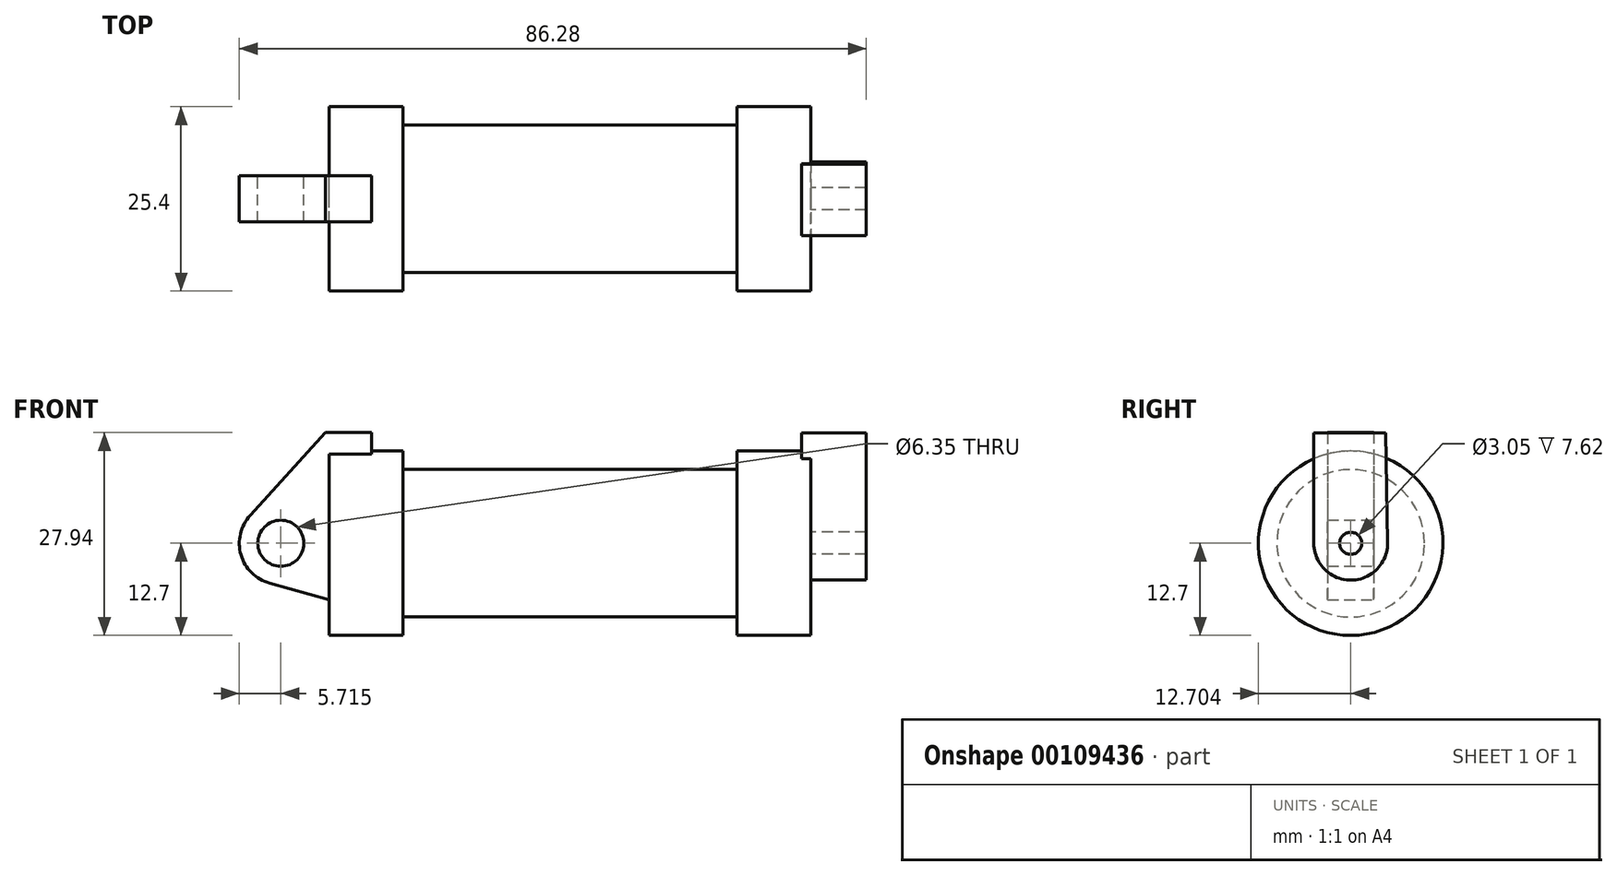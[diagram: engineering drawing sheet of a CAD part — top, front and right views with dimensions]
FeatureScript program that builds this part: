
annotation { "Feature Type Name" : "Feature", "Feature Type Description" : "" }
export const myFeature = defineFeature(function(context is Context, id is Id, definition is map)
    precondition{}
    {
        {
            var Q0;
            Q0=qCreatedBy(makeId("Front.planeOp"),FACE);
            var sketch = newSketch(context, id + "F0", { "sketchPlane" : qUnion([Q0])});
            skLineSegment(sketch, "E0", {"start": v(0, 0) * mm, "end": v(0, 12.7) * mm});
            skLineSegment(sketch, "E1", {"start": v(0, 12.7) * mm, "end": v(10.16, 12.7) * mm});
            skLineSegment(sketch, "E2", {"start": v(10.16, 12.7) * mm, "end": v(10.16, 10.16) * mm});
            skLineSegment(sketch, "E3", {"start": v(10.16, 10.16) * mm, "end": v(56.13, 10.16) * mm});
            skLineSegment(sketch, "E4", {"start": v(56.13, 10.16) * mm, "end": v(56.13, 12.7) * mm});
            skLineSegment(sketch, "E5", {"start": v(56.13, 12.7) * mm, "end": v(66.3, 12.7) * mm});
            skLineSegment(sketch, "E6", {"start": v(66.3, 12.7) * mm, "end": v(66.3, 0) * mm});
            skLineSegment(sketch, "E7", {"start": v(66.3, 0) * mm, "end": v(0, 0) * mm});
            skLineSegment(sketch, "E8", {"start": v(5.84, 15.24) * mm, "end": v(-0.5, 15.24) * mm});
            skLineSegment(sketch, "E9", {"start": v(-0.5, 15.24) * mm, "end": v(-10.88, 3.85) * mm});
            skLineSegment(sketch, "E10", {"start": v(0, 0) * mm, "end": v(-6.65, 0) * mm});
            skCircle(sketch, "E11", {"center": v(-6.65, 0) * mm, "radius": 5.72 * mm});
            skCircle(sketch, "E12", {"center": v(-6.65, 0) * mm, "radius": 3.18 * mm});
            skLineSegment(sketch, "E13", {"start": v(5.84, 15.24) * mm, "end": v(5.84, -9.4) * mm});
            skLineSegment(sketch, "E14", {"start": v(5.84, -9.4) * mm, "end": v(-8.18, -5.5) * mm});
            skSolve(sketch);
        }
        {
            var Q0;
            {var subQ0=sQuery(id+"F0.wireOp",EDGE,"E2");Q0=makeQuery(id+"F0.imprint","IMPRINT",FACE,{"disambiguationData":[TD([[makeQuery(id+"F0.imprint","IMPRINT",EDGE,{"derivedFrom":subQ0}),-1.0]])]});}
            var Q1;
            {var subQ0=sQuery(id+"F0.wireOp",EDGE,"E0");Q1=makeQuery(id+"F0.imprint","IMPRINT",FACE,{"disambiguationData":[TD([[makeQuery(id+"F0.imprint","IMPRINT",EDGE,{"derivedFrom":subQ0}),-1.0]])]});}
            var Q2;
            Q2=sQuery(id+"F0.wireOp",EDGE,"E7");
            revolve(context, id + "F1", {"entities" : qUnion([Q0, Q1]), "axis" : qUnion([Q2]), "revolveType" : RevolveType.FULL});
        }
        {
            var Q0;
            {var subQ3=sQuery(id+"F0.wireOp",EDGE,"E0");Q0=makeQuery(id+"F0.imprint","IMPRINT",FACE,{"disambiguationData":[TD([[makeQuery(id+"F0.imprint","IMPRINT",EDGE,{"derivedFrom":subQ3}),1.0]])]});}
            var Q1;
            {var subQ4=sQuery(id+"F0.wireOp",EDGE,"E12");Q1=makeQuery(id+"F0.imprint","IMPRINT",FACE,{"disambiguationData":[TD([[makeQuery(id+"F0.imprint","IMPRINT",EDGE,{"derivedFrom":subQ4}),-1.0]])]});}
            var Q2;
            {var subQ0=sQuery(id+"F0.wireOp",EDGE,"E14");Q2=makeQuery(id+"F0.imprint","IMPRINT",FACE,{"disambiguationData":[TD([[makeQuery(id+"F0.imprint","IMPRINT",EDGE,{"derivedFrom":subQ0}),-1.0]])]});}
            var Q3;
            {var subQ0=sQuery(id+"F0.wireOp",EDGE,"E0");Q3=makeQuery(id+"F0.imprint","IMPRINT",FACE,{"disambiguationData":[TD([[makeQuery(id+"F0.imprint","IMPRINT",EDGE,{"derivedFrom":subQ0}),-1.0]])]});}
            extrude(context, id + "F2", {"entities" : qUnion([Q0, Q1, Q2, Q3]), "operationType" : NewBodyOperationType.ADD, "endBound" : BoundingType.SYMMETRIC, "depth" : 6.35 * mm});
        }
        {
            var Q0;
            Q0=makeQuery(id+"F1.opRevolve","SWEPT_FACE",FACE,{"disambiguationData":[OSD([sQuery(id+"F0.wireOp",EDGE,"E6")])]});
            var sketch = newSketch(context, id + "F3", { "sketchPlane" : qUnion([Q0])});
            skSolve(sketch);
        }
        {
            var Q0;
            Q0=makeQuery(id+"F3.imprint","IMPRINT",FACE,{"disambiguationData":[TD([[makeQuery(id+"F3.imprint","IMPRINT",EDGE,{"derivedFrom":makeQuery(id+"F1.opRevolve","SWEPT_EDGE",EDGE,{"disambiguationData":[OSD([sQuery(id+"F0.wireOp",EDGE,"E5"),sQuery(id+"F0.wireOp",EDGE,"E6")])]})}),1.0]])]});
            var sketch = newSketch(context, id + "F4", { "sketchPlane" : qUnion([Q0])});
            skCircle(sketch, "E15", {"center": v(0, 0) * mm, "radius": 5.08 * mm});
            skLineSegment(sketch, "E16", {"start": v(-5.08, 0) * mm, "end": v(-5.08, 15.19) * mm});
            skLineSegment(sketch, "E17", {"start": v(5.08, 0.1) * mm, "end": v(4.81, 15.24) * mm});
            skLineSegment(sketch, "E18", {"start": v(4.81, 15.24) * mm, "end": v(-5.08, 15.19) * mm});
            skCircle(sketch, "E19", {"center": v(0, 0) * mm, "radius": 1.52 * mm});
            skSolve(sketch);
        }
        {
            var Q0;
            Q0 = qSketchRegion(id + "F4", true);
            extrude(context, id + "F5", {"entities" : qUnion([Q0]), "operationType" : NewBodyOperationType.ADD, "depth" : 7.62 * mm, "hasSecondDirection" : true, "secondDirectionOppositeDirection" : true, "secondDirectionDepth" : 1.27 * mm});
        }
        {
            var Q0;
            Q0=makeQuery(id+"F5.opExtrude","SWEPT_FACE",FACE,{"disambiguationData":[OSD([sQuery(id+"F4.wireOp",EDGE,"E18")])]});
            var sketch = newSketch(context, id + "F6", { "sketchPlane" : qUnion([Q0])});
            skCircle(sketch, "E20", {"center": v(69.04, -0.72) * mm, "radius": 1.52 * mm});
            skSolve(sketch);
        }
        {
            var Q0;
            Q0 = qSketchRegion(id + "F6", true);
            extrude(context, id + "F7", {"entities" : qUnion([Q0]), "operationType" : NewBodyOperationType.ADD, "oppositeDirection" : true, "depth" : 9.7 * mm});
        }
        {
            var Q0;
            Q0=makeQuery(id+"F5.opExtrude","SWEPT_FACE",FACE,{"disambiguationData":[OSD([sQuery(id+"F4.wireOp",EDGE,"E18")])]});
            var sketch = newSketch(context, id + "F8", { "sketchPlane" : qUnion([Q0])});
            skCircle(sketch, "E21", {"center": v(69.5, 0.04) * mm, "radius": 1.52 * mm});
            skSolve(sketch);
        }
        {
            var Q0;
            Q0 = qSketchRegion(id + "F8", true);
            extrude(context, id + "F9", {"entities" : qUnion([Q0]), "operationType" : NewBodyOperationType.ADD, "oppositeDirection" : true, "depth" : 6.88 * mm});
        }
    });
